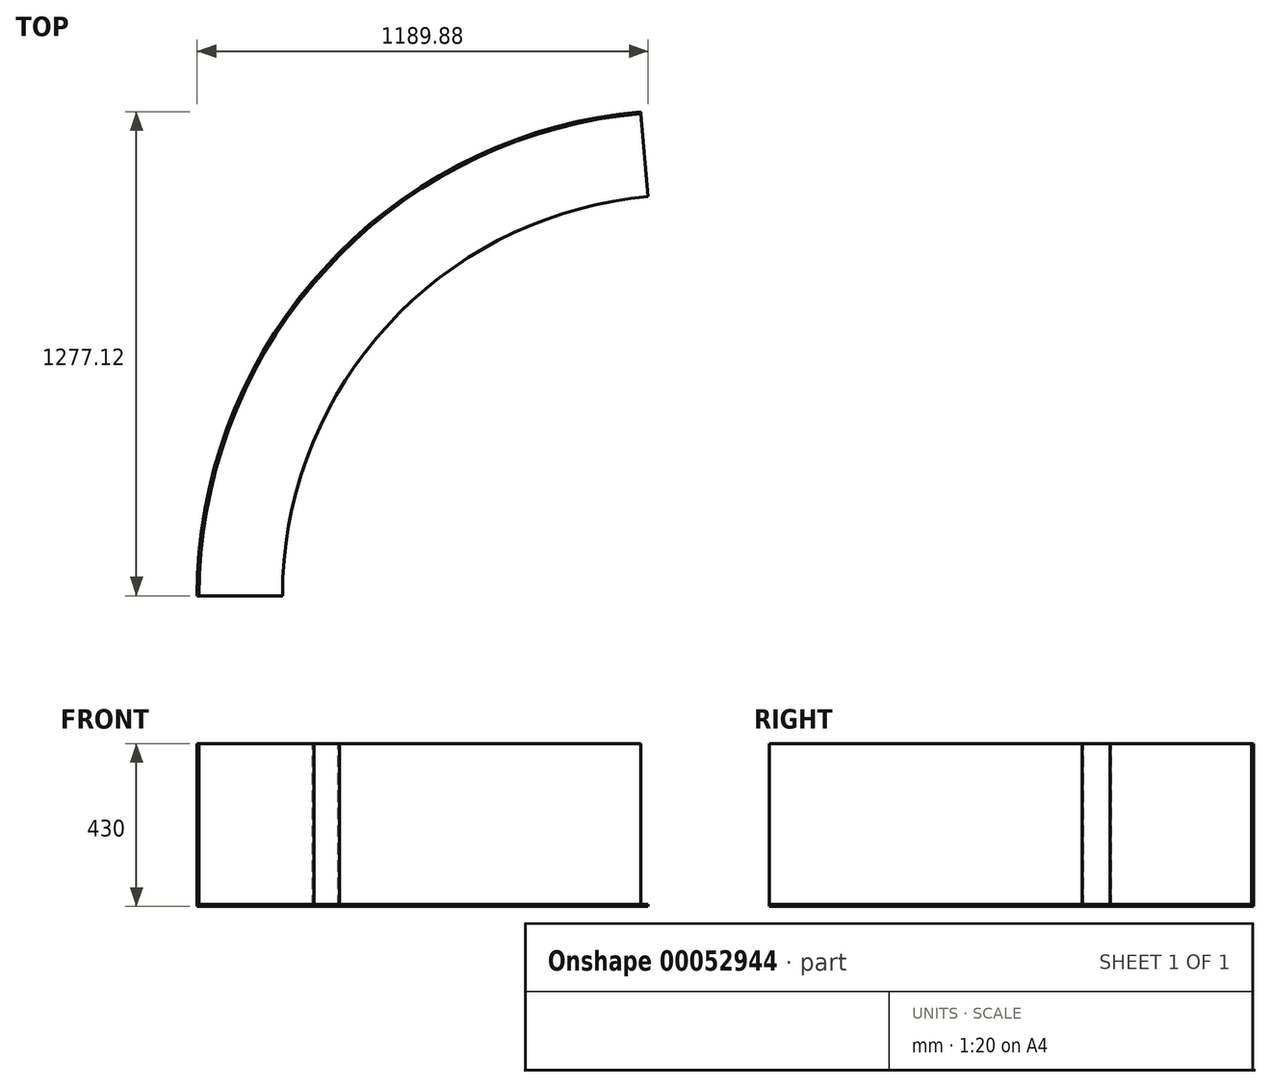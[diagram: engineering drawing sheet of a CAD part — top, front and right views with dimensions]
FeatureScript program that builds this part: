
annotation { "Feature Type Name" : "Feature", "Feature Type Description" : "" }
export const myFeature = defineFeature(function(context is Context, id is Id, definition is map)
    precondition{}
    {
        {
            var Q0;
            Q0=qCreatedBy(makeId("Front.planeOp"),FACE);
            var sketch = newSketch(context, id + "F0", { "sketchPlane" : qUnion([Q0])});
            skLineSegment(sketch, "E0", {"start": v(0, 0) * mm, "end": v(-225, 0) * mm});
            skLineSegment(sketch, "E1", {"start": v(-225, 0) * mm, "end": v(-225, 430) * mm});
            skLineSegment(sketch, "E2.0", {"start": v(-220, 5) * mm, "end": v(-220, 430) * mm});
            skLineSegment(sketch, "E2.1", {"start": v(0, 5) * mm, "end": v(-220, 5) * mm});
            skLineSegment(sketch, "E3", {"start": v(-225, 430) * mm, "end": v(-220, 430) * mm});
            skLineSegment(sketch, "E4", {"start": v(0, 5) * mm, "end": v(0, 0) * mm});
            skSolve(sketch);
        }
        {
            var Q0;
            Q0=qCreatedBy(makeId("Top.planeOp"),FACE);
            var sketch = newSketch(context, id + "F1", { "sketchPlane" : qUnion([Q0])});
            skArc(sketch, "E5", {"start": v(945.27, 1277.12) * mm, "mid": v(512.52, 1160.63) * mm, "end": v(146.3, 902.31) * mm});
            skLineSegment(sketch, "E6", {"start": v(1057, 0) * mm, "end": v(78.75, 828.58) * mm, "construction": true});
            skLineSegment(sketch, "E7", {"start": v(1057, 0) * mm, "end": v(146.3, 902.31) * mm, "construction": true});
            skLineSegment(sketch, "E8", {"start": v(78.75, 828.58) * mm, "end": v(146.3, 902.31) * mm});
            skLineSegment(sketch, "E9", {"start": v(1057, 0) * mm, "end": v(112.53, 865.45) * mm, "construction": true});
            skArc(sketch, "E10.trimOffspring", {"start": v(78.75, 828.58) * mm, "mid": v(-146.67, 441.25) * mm, "end": v(-225, 0) * mm});
            skLineSegment(sketch, "E11", {"start": v(1057, 0) * mm, "end": v(945.27, 1277.12) * mm, "construction": true});
            skLineSegment(sketch, "E12", {"start": v(1057, 0) * mm, "end": v(-225, 0) * mm, "construction": true});
            skSolve(sketch);
        }
        {
            var Q0;
            Q0 = qSketchRegion(id + "F0", true);
            var Q1;
            Q1=sQuery(id+"F1.wireOp",EDGE,"E5");
            var Q2;
            Q2=sQuery(id+"F1.wireOp",EDGE,"E8");
            var Q3;
            Q3=sQuery(id+"F1.wireOp",EDGE,"E10.trimOffspring");
            sweep(context, id + "F2", {"profiles" : qUnion([Q0]), "path" : qUnion([Q1, Q2, Q3])});
        }
    });
